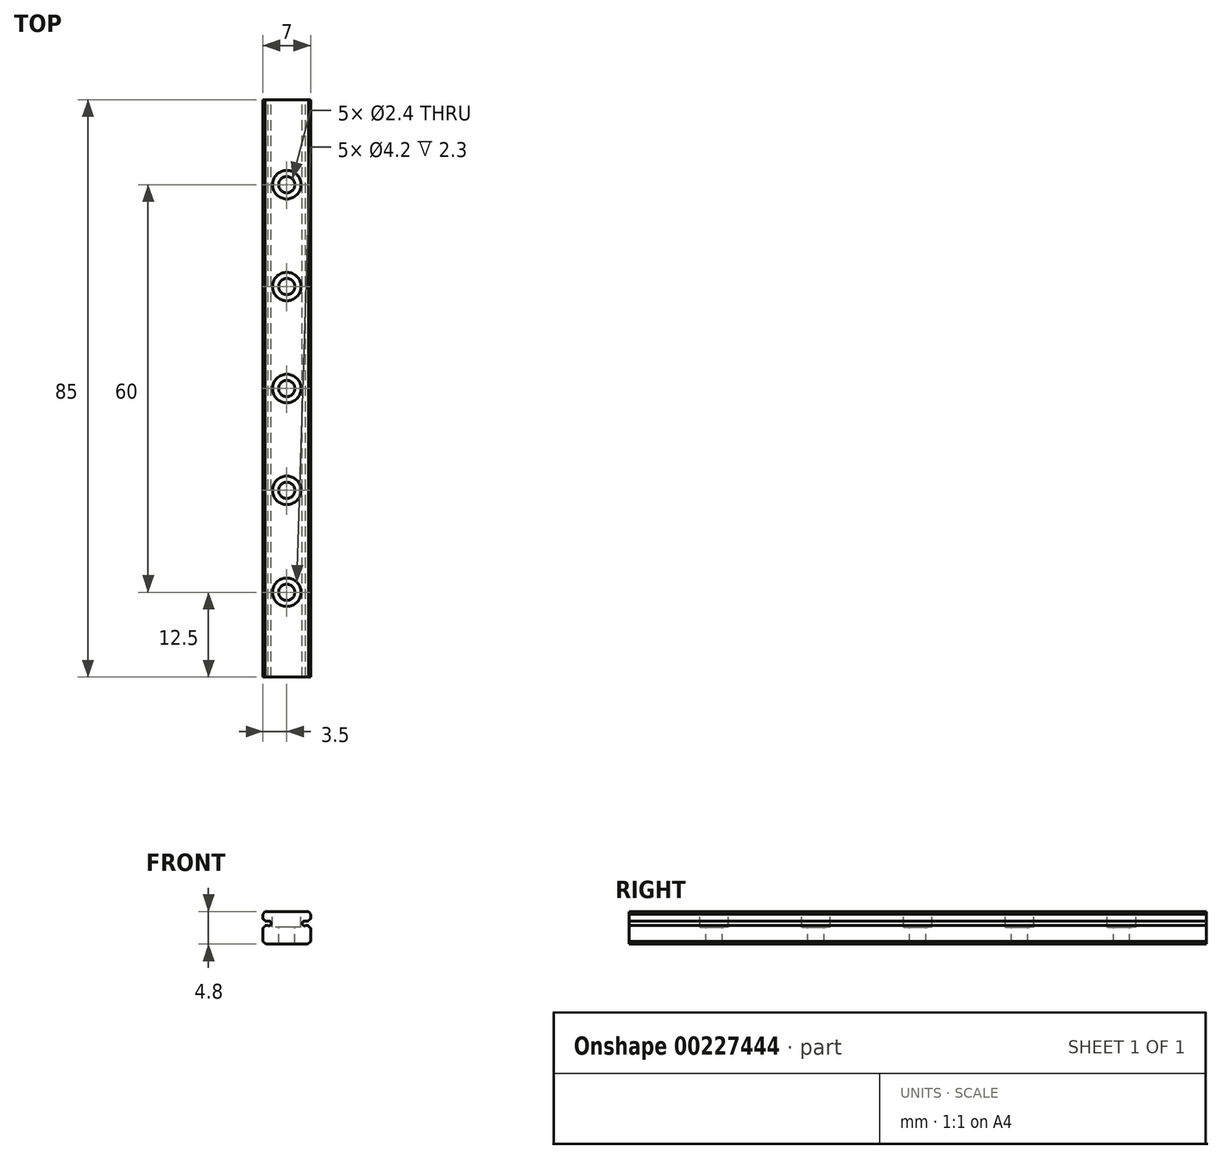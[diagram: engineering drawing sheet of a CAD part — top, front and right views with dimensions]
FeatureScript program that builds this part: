
annotation { "Feature Type Name" : "Feature", "Feature Type Description" : "" }
export const myFeature = defineFeature(function(context is Context, id is Id, definition is map)
    precondition{}
    {
        {
            var Q0;
            Q0=qCreatedBy(makeId("Front.planeOp"),FACE);
            var sketch = newSketch(context, id + "F0", { "sketchPlane" : qUnion([Q0])});
            skLineSegment(sketch, "E0.bottom", {"start": v(3.5, 0) * mm, "end": v(-3.5, 0) * mm});
            skLineSegment(sketch, "E0.top", {"start": v(3.5, 4.8) * mm, "end": v(-3.5, 4.8) * mm});
            skLineSegment(sketch, "E0.left", {"start": v(3.5, 3.76) * mm, "end": v(3.5, 4.8) * mm});
            skLineSegment(sketch, "E1", {"start": v(-3.5, 3.06) * mm, "end": v(3.5, 3.06) * mm, "construction": true});
            skCircle(sketch, "E2", {"center": v(2.63, 3.06) * mm, "radius": 0.35 * mm});
            skPoint(sketch, "E3", {"position": v(3.77, 3.06) * mm});
            skArc(sketch, "E4", {"start": v(3.18, 3.43) * mm, "mid": v(3.3, 3.57) * mm, "end": v(3.45, 3.67) * mm, "construction": true});
            skLineSegment(sketch, "E5", {"start": v(3.1, 3.38) * mm, "end": v(2.77, 3.38) * mm});
            skArc(sketch, "E6.filletArc", {"start": v(3.1, 3.38) * mm, "mid": v(3.14, 3.4) * mm, "end": v(3.18, 3.43) * mm});
            skPoint(sketch, "E7.newPointB", {"position": v(3.5, 0) * mm});
            skArc(sketch, "E7.filletArc", {"start": v(3.45, 3.67) * mm, "mid": v(3.49, 3.71) * mm, "end": v(3.5, 3.76) * mm});
            skLineSegment(sketch, "E8.MirrorCS", {"start": v(3.1, 2.73) * mm, "end": v(2.77, 2.73) * mm});
            skArc(sketch, "E9.MirrorCS", {"start": v(3.1, 2.73) * mm, "mid": v(3.14, 2.72) * mm, "end": v(3.18, 2.69) * mm});
            skArc(sketch, "E10.MirrorCS", {"start": v(3.18, 2.69) * mm, "mid": v(3.3, 2.54) * mm, "end": v(3.45, 2.44) * mm, "construction": true});
            skArc(sketch, "E11.MirrorCS", {"start": v(3.45, 2.44) * mm, "mid": v(3.49, 2.4) * mm, "end": v(3.5, 2.35) * mm});
            skArc(sketch, "E12", {"start": v(3.18, 2.69) * mm, "mid": v(3.3, 2.54) * mm, "end": v(3.45, 2.44) * mm});
            skLineSegment(sketch, "E13", {"start": v(3.5, 2.35) * mm, "end": v(3.5, 0) * mm});
            skArc(sketch, "E14", {"start": v(3.18, 3.43) * mm, "mid": v(3.3, 3.57) * mm, "end": v(3.45, 3.67) * mm});
            skArc(sketch, "E15.MirrorCS", {"start": v(-3.45, 3.67) * mm, "mid": v(-3.49, 3.71) * mm, "end": v(-3.5, 3.76) * mm});
            skArc(sketch, "E16.MirrorCS", {"start": v(-3.18, 3.43) * mm, "mid": v(-3.3, 3.57) * mm, "end": v(-3.45, 3.67) * mm, "construction": true});
            skArc(sketch, "E17.MirrorCS", {"start": v(-3.1, 3.38) * mm, "mid": v(-3.14, 3.4) * mm, "end": v(-3.18, 3.43) * mm});
            skLineSegment(sketch, "E18.MirrorCS", {"start": v(-3.1, 3.38) * mm, "end": v(-2.77, 3.38) * mm});
            skCircle(sketch, "E19.MirrorC", {"center": v(-2.63, 3.06) * mm, "radius": 0.35 * mm});
            skLineSegment(sketch, "E20.MirrorCS", {"start": v(-3.1, 2.73) * mm, "end": v(-2.77, 2.73) * mm});
            skArc(sketch, "E21.MirrorCS", {"start": v(-3.1, 2.73) * mm, "mid": v(-3.14, 2.72) * mm, "end": v(-3.18, 2.69) * mm});
            skArc(sketch, "E22.MirrorCS", {"start": v(-3.18, 2.69) * mm, "mid": v(-3.3, 2.54) * mm, "end": v(-3.45, 2.44) * mm, "construction": true});
            skArc(sketch, "E23.MirrorCS", {"start": v(-3.45, 2.44) * mm, "mid": v(-3.49, 2.4) * mm, "end": v(-3.5, 2.35) * mm});
            skArc(sketch, "E24", {"start": v(-3.45, 3.67) * mm, "mid": v(-3.3, 3.57) * mm, "end": v(-3.18, 3.43) * mm});
            skArc(sketch, "E25", {"start": v(-3.18, 2.69) * mm, "mid": v(-3.3, 2.54) * mm, "end": v(-3.45, 2.44) * mm});
            skLineSegment(sketch, "E26", {"start": v(-3.5, 4.8) * mm, "end": v(-3.5, 3.76) * mm});
            skLineSegment(sketch, "E27", {"start": v(-3.5, 2.35) * mm, "end": v(-3.5, 0) * mm});
            skSolve(sketch);
        }
        {
            var Q0;
            Q0=makeQuery(id+"F0.imprint","IMPRINT",FACE,{"disambiguationData":[TD([[makeQuery(id+"F0.imprint","IMPRINT",EDGE,{"derivedFrom":sQuery(id+"F0.wireOp",EDGE,"E0.bottom")}),-1.0]])]});
            extrude(context, id + "F1", {"entities" : qUnion([Q0]), "depth" : 85 * mm, "symmetric" : true});
        }
        {
            var Q0;
            Q0=makeQuery(id+"F1.opExtrude","SWEPT_EDGE",EDGE,{"disambiguationData":[OSD([sQuery(id+"F0.wireOp",EDGE,"E0.top"),sQuery(id+"F0.wireOp",EDGE,"E0.left")])]});
            var Q1;
            Q1=makeQuery(id+"F1.opExtrude","SWEPT_EDGE",EDGE,{"disambiguationData":[OSD([sQuery(id+"F0.wireOp",EDGE,"E0.top"),sQuery(id+"F0.wireOp",EDGE,"E0.right")])]});
            chamfer(context, id + "F2", {"entities" : qUnion([Q0, Q1]), "chamferType" : ChamferType.TWO_OFFSETS, "width1" : 0.3 * mm, "oppositeDirection" : false, "width2" : 0.39 * mm, "tangentPropagation" : true});
        }
        {
            var Q0;
            Q0=makeQuery(id+"F1.opExtrude","SWEPT_EDGE",EDGE,{"disambiguationData":[OSD([sQuery(id+"F0.wireOp",EDGE,"E0.bottom"),sQuery(id+"F0.wireOp",EDGE,"E13")])]});
            var Q1;
            Q1=makeQuery(id+"F1.opExtrude","SWEPT_EDGE",EDGE,{"disambiguationData":[OSD([sQuery(id+"F0.wireOp",EDGE,"E0.bottom"),sQuery(id+"F0.wireOp",EDGE,"E0.right")])]});
            chamfer(context, id + "F3", {"entities" : qUnion([Q0, Q1]), "width" : 0.4 * mm, "tangentPropagation" : true});
        }
        {
            var Q0;
            Q0=makeQuery(id+"F1.opExtrude","SWEPT_FACE",FACE,{"disambiguationData":[OSD([sQuery(id+"F0.wireOp",EDGE,"E0.top")])]});
            var sketch = newSketch(context, id + "F4", { "sketchPlane" : qUnion([Q0])});
            skPoint(sketch, "E28", {"position": v(0, 30) * mm});
            skPoint(sketch, "E29.0.1.0", {"position": v(0, 15) * mm});
            skPoint(sketch, "E29.0.2.0", {"position": v(0, 0) * mm});
            skPoint(sketch, "E29.0.3.0", {"position": v(0, -15) * mm});
            skPoint(sketch, "E29.0.4.0", {"position": v(0, -30) * mm});
            skLineSegment(sketch, "E29.direction2", {"start": v(0, 30) * mm, "end": v(0, 15) * mm, "construction": true});
            skSolve(sketch);
        }
        {
            var Q0;
            Q0=sQuery(id+"F4.wireOp",VERTEX,"E28");
            var Q1;
            Q1=sQuery(id+"F4.wireOp",VERTEX,"E29.0.1.0");
            var Q2;
            Q2=sQuery(id+"F4.wireOp",VERTEX,"E29.0.2.0");
            var Q3;
            Q3=sQuery(id+"F4.wireOp",VERTEX,"E29.0.3.0");
            var Q4;
            Q4=sQuery(id+"F4.wireOp",VERTEX,"E29.0.4.0");
            var Q5;
            Q5=makeQuery(id+"F1.opExtrude","SWEPT_BODY",BODY,{"disambiguationData":[OSD([sQuery(id+"F0.wireOp",EDGE,"E0.bottom"),sQuery(id+"F0.wireOp",EDGE,"E0.top"),sQuery(id+"F0.wireOp",EDGE,"E0.left"),sQuery(id+"F0.wireOp",EDGE,"E2"),sQuery(id+"F0.wireOp",EDGE,"E5"),sQuery(id+"F0.wireOp",EDGE,"E6.filletArc"),sQuery(id+"F0.wireOp",EDGE,"E7.filletArc"),sQuery(id+"F0.wireOp",EDGE,"E8.MirrorCS"),sQuery(id+"F0.wireOp",EDGE,"E9.MirrorCS"),sQuery(id+"F0.wireOp",EDGE,"E11.MirrorCS"),sQuery(id+"F0.wireOp",EDGE,"E12"),sQuery(id+"F0.wireOp",EDGE,"E13"),sQuery(id+"F0.wireOp",EDGE,"E14"),sQuery(id+"F0.wireOp",EDGE,"E15.MirrorCS"),sQuery(id+"F0.wireOp",EDGE,"E17.MirrorCS"),sQuery(id+"F0.wireOp",EDGE,"E18.MirrorCS"),sQuery(id+"F0.wireOp",EDGE,"E19.MirrorC"),sQuery(id+"F0.wireOp",EDGE,"E20.MirrorCS"),sQuery(id+"F0.wireOp",EDGE,"E21.MirrorCS"),sQuery(id+"F0.wireOp",EDGE,"E23.MirrorCS"),sQuery(id+"F0.wireOp",EDGE,"E24"),sQuery(id+"F0.wireOp",EDGE,"E25"),sQuery(id+"F0.wireOp",EDGE,"E26"),sQuery(id+"F0.wireOp",EDGE,"E27")])]});
            hole(context, id + "F5", {"style" : HoleStyle.C_BORE, "endStyle" : HoleEndStyle.THROUGH, "holeDiameter" : 2.4 * mm, "cBoreDiameter" : 4.2 * mm, "cBoreDepth" : 2.3 * mm, "tappedDepth" : 12 * mm, "tapClearance" : 3, "locations" : qUnion([Q0, Q1, Q2, Q3, Q4]), "scope" : qUnion([Q5])});
        }
    });
